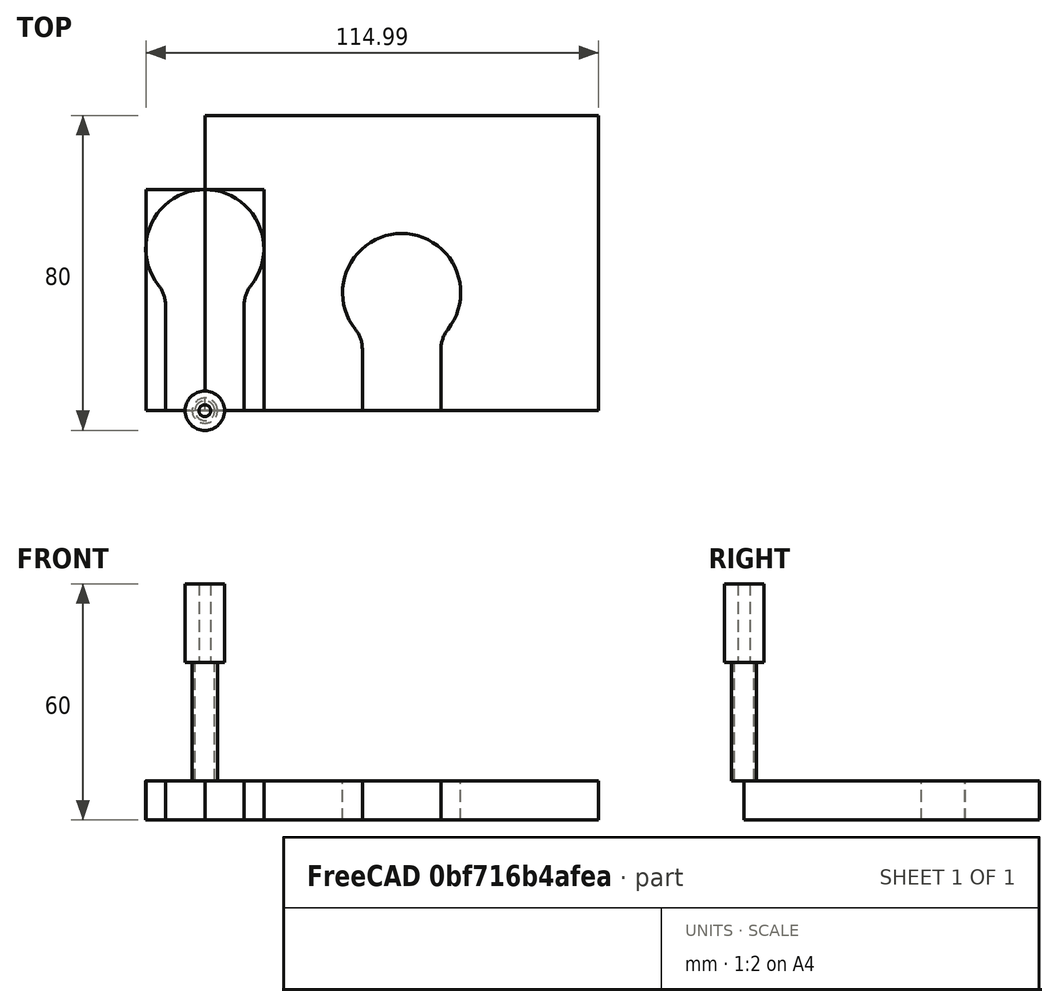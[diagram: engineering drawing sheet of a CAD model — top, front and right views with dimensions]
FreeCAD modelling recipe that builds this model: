
FCSTD DOCUMENT  (FreeCAD 0.19R14555 (Git shallow))
Label: Keyhole
License: All rights reserved
LicenseURL: http://en.wikipedia.org/wiki/All_rights_reserved
objects: Part::FeaturePython×8, Path::FeaturePython×8, App::DocumentObjectGroup×4, Sketcher::SketchObject×2, PartDesign::Pad×2, App::FeaturePython×2, PartDesign::Fillet×2, PartDesign::Body×2, App::Part×2, Path::FeatureCompoundPython×2, Mesh::FeaturePython×1
note: 23 computed .brp shape members not serialized (recipe doc carries the construction recipe); baked Part::Feature solids carry a one-line shape summary decoded from their .brp

FEATURE [Sketcher::SketchObject] Sketch
  FullyConstrained = true
  MapMode = 5
  Support = -> [XY_Plane001]
  sketch-geometry (8):
    g0: LineSegment StartX=0 StartY=75 StartZ=0 EndX=100 EndY=75 EndZ=0
    g1: LineSegment StartX=100 StartY=75 StartZ=0 EndX=100 EndY=0 EndZ=0
    g2: LineSegment StartX=100 StartY=0 StartZ=0 EndX=60 EndY=0 EndZ=0
    g3: LineSegment StartX=0 StartY=0 StartZ=0 EndX=0 EndY=75 EndZ=0
    g4: ArcOfCircle CenterX=50 CenterY=30 CenterZ=0 NormalX=0 NormalY=0 NormalZ=1 AngleXU=0 Radius=15 StartAngle=5.44212 EndAngle=10.2658
    g5: LineSegment StartX=40 StartY=0 StartZ=0 EndX=40 EndY=18.8197 EndZ=0
    g6: LineSegment StartX=60 StartY=0 StartZ=0 EndX=60 EndY=18.8197 EndZ=0
    g7: LineSegment StartX=40 StartY=0 StartZ=0 EndX=0 EndY=0 EndZ=0
  constraints (23):
    c: Coincident(g0,g1)
    c: Coincident(g1,g2)
    c: Coincident(g7,g3)
    c: Coincident(g3,g0)
    c: Horizontal(g0)
    c: Horizontal(g2)
    c: Vertical(g1)
    c: Vertical(g3)
    c: Coincident(g7,g-1)
    c: DistanceX(g7,g2) = 100
    c: DistanceY(g3,g3) = 75
    c: Diameter(g4) = 30
    c: DistanceX(g7,g4) = 50
    c: DistanceY(g7,g4) = 30
    c: Perpendicular(g2,g5)
    c: Perpendicular(g2,g6)
    c: DistanceX(g7,g5) = 40
    c: DistanceX(g7,g6) = 60
    c: Coincident(g4,g6)
    c: Coincident(g4,g5)
    c: Coincident(g2,g6)
    c: Coincident(g7,g5)
    c: Tangent(g2,g7)
FEATURE [PartDesign::Pad] Pad
  Direction = (1,1,1)
  Length = 10
  Length2 = 100
  Profile = -> Sketch
  Refine = true
  Reversed = true
  Type = 0
FEATURE [App::FeaturePython] SetupSheet  # Path/CAM operation (typed FeaturePython)
  ClearanceHeightExpression = OpStockZMax+SetupSheet.ClearanceHeightOffset
  ClearanceHeightOffset = 5
  CoolantMode = 0
  CoolantModes = None | Flood | Mist
  FinalDepthExpression = OpFinalDepth
  HorizRapid = 0
  SafeHeightExpression = OpStockZMax+SetupSheet.SafeHeightOffset
  SafeHeightOffset = 3
  StartDepthExpression = OpStartDepth
  StepDownExpression = OpToolDiameter
  VertRapid = 0
FEATURE [Part::FeaturePython] ToolBit001  label="5mm Endmill"  # Path/CAM toolbit (typed FeaturePython)
  BitPropertyNames = Chipload | CuttingEdgeHeight | Diameter | Flutes | Length | Material | ShankDiameter
  BitShape = /app/freecad/Mod/Path/Tools/Shape/endmill.fcstd
  Chipload = 0
  CuttingEdgeHeight = 30
  Diameter = 5
  File = <userpath>/Documents/CNCRouter/FreeCAD/Bit/5mm_Endmill.fctb
  Flutes = 0
  Length = 50
  Material = 0
  ShankDiameter = 3
  ShapeName = endmill
FEATURE [Path::FeaturePython] _mm_Endmill  label="5mm Endmill001"  # Path/CAM operation (typed FeaturePython)
  HorizFeed = 10
  HorizRapid = 0
  SpindleDir = 0
  SpindleSpeed = 5000
  Tool = -> ToolBit001
  ToolNumber = 1
  VertFeed = 10
  VertRapid = 0
  expr: VertRapid = SetupSheet.VertRapid
  expr: HorizRapid = SetupSheet.HorizRapid
FEATURE [Part::FeaturePython] Stock001  # WARN: FeaturePython — macro-defined, semantics opaque (R4)
  Height = 10
  Length = 100
  Placement = pos=(0,0,-10) rot=(0,0,1;0rad)
  StockType = CreateBox
  Width = 75
FEATURE [Mesh::FeaturePython] CutMaterial  # WARN: FeaturePython — macro-defined, semantics opaque (R4)
FEATURE [PartDesign::Fillet] Fillet
  Base = -> Pad [Edge20,Edge17]
  BaseFeature = -> Pad
  Radius = 8
  SupportTransform = false
FEATURE [PartDesign::Body] Body
  Group = -> [Sketch,Pad,Fillet]
  Origin = -> Origin001
  Tip = -> Fillet
FEATURE [App::Part] Part  label="Female"
  Group = -> [Body]
  Origin = -> Origin
FEATURE [Part::FeaturePython] Clone  label="Model-Part"  # Draft clone (typed FeaturePython)
  AttacherType = Attacher::AttachEngine3D
  Fuse = false
  Objects = -> [Part]
  PathResource = Model
  Scale = (1,1,1)
FEATURE [App::DocumentObjectGroup] Model
  Group = -> [Clone]
FEATURE [Sketcher::SketchObject] Sketch001
  FullyConstrained = false
  MapMode = 5
  Support = -> [XY_Plane003]
  sketch-geometry (4):
    g0: LineSegment StartX=9.995 StartY=30 StartZ=0 EndX=9.995 EndY=0 EndZ=0
    g1: LineSegment StartX=9.995 StartY=0 StartZ=0 EndX=-9.995 EndY=0 EndZ=0
    g2: LineSegment StartX=-9.995 StartY=0 StartZ=0 EndX=-9.995 EndY=30 EndZ=0
    g3: ArcOfCircle CenterX=0 CenterY=41.1781 CenterZ=0 NormalX=0 NormalY=0 NormalZ=1 AngleXU=0 Radius=14.995 StartAngle=5.44197 EndAngle=10.266
  constraints (9):
    c: Coincident(g0,g1)
    c: Coincident(g1,g2)
    c: Horizontal(g1)
    c: Vertical(g0)
    c: Vertical(g2)
    c: Symmetric(g1,g1,g-1)
    c: DistanceY(g0,g0) = 30
    c: DistanceX(g1,g1) = 19.99
    c: Diameter(g3) = 29.99
FEATURE [PartDesign::Pad] Pad001
  Direction = (1,1,1)
  Length = 10
  Length2 = 100
  Profile = -> Sketch001
  Reversed = true
  Type = 0
FEATURE [PartDesign::Fillet] Fillet001
  Base = -> Pad001 [Edge8,Edge1]
  BaseFeature = -> Pad001
  Radius = 8
  SupportTransform = false
FEATURE [PartDesign::Body] Body001
  Group = -> [Sketch001,Pad001,Fillet001]
  Origin = -> Origin003
  Tip = -> Fillet001
FEATURE [App::Part] Part001  label="Male"
  Group = -> [Body001]
  Origin = -> Origin002
FEATURE [App::FeaturePython] SetupSheet001  # Path/CAM operation (typed FeaturePython)
  ClearanceHeightExpression = OpStockZMax+SetupSheet001.ClearanceHeightOffset
  ClearanceHeightOffset = 5
  CoolantMode = 0
  CoolantModes = None | Flood | Mist
  FinalDepthExpression = OpFinalDepth
  HorizRapid = 0
  SafeHeightExpression = OpStockZMax+SetupSheet001.SafeHeightOffset
  SafeHeightOffset = 3
  StartDepthExpression = OpStartDepth
  StepDownExpression = OpToolDiameter
  VertRapid = 0
FEATURE [Part::FeaturePython] Clone001  label="Model-Male"  # Draft clone (typed FeaturePython)
  AttacherType = Attacher::AttachEngine3D
  Fuse = false
  Objects = -> [Part001]
  PathResource = Model
  Scale = (1,1,1)
FEATURE [App::DocumentObjectGroup] Model001
  Group = -> [Clone001]
FEATURE [Part::FeaturePython] Stock002  # WARN: FeaturePython — macro-defined, semantics opaque (R4)
  Height = 10
  Length = 29.98
  Placement = pos=(-14.9877,0,-10) rot=(0,0,1;0rad)
  StockType = CreateBox
  Width = 56.1423
FEATURE [Part::FeaturePython] ToolBit002  label="6.4mm Endmill"  # Path/CAM toolbit (typed FeaturePython)
  BitPropertyNames = Chipload | CuttingEdgeHeight | Diameter | Flutes | Length | Material | ShankDiameter
  BitShape = /app/freecad/Mod/Path/Tools/Shape/endmill.fcstd
  Chipload = 0
  CuttingEdgeHeight = 30
  Diameter = 6.4
  File = <userpath>/Documents/MensShed/FreeCAD/Bit/6.4mm_Endmill.fctb
  Flutes = 0
  Length = 50
  Material = 0
  ShankDiameter = 10
  ShapeName = endmill
FEATURE [Part::FeaturePython] ToolBit  label="6.4mm Endmill002"  # Path/CAM toolbit (typed FeaturePython)
  BitPropertyNames = Chipload | CuttingEdgeHeight | Diameter | Flutes | Length | Material | ShankDiameter
  BitShape = /app/freecad/Mod/Path/Tools/Shape/endmill.fcstd
  Chipload = 0
  CuttingEdgeHeight = 30
  Diameter = 6.4
  Flutes = 0
  Length = 50
  Material = 0
  ShankDiameter = 10
  ShapeName = endmill
FEATURE [Path::FeaturePython] __4mm_Endmill  label="6.4mm Endmill001"  # Path/CAM operation (typed FeaturePython)
  HorizFeed = 10
  HorizRapid = 0
  SpindleDir = 0
  SpindleSpeed = 5000
  Tool = -> ToolBit
  ToolNumber = 1
  VertFeed = 10
  VertRapid = 0
  expr: HorizRapid = SetupSheet001.HorizRapid
  expr: VertRapid = SetupSheet001.VertRapid
FEATURE [App::DocumentObjectGroup] Tools001
  Group = -> [__4mm_Endmill]
FEATURE [Path::FeaturePython] Profile001  # Path/CAM operation (typed FeaturePython)
  Active = true
  AttemptInverseAngle = false
  ClearanceHeight = 0
  Direction = 0
  EnableRotation = 0
  FinalDepth = 0
  HandleMultipleFeatures = 0
  InverseAngle = false
  JoinType = 0
  LimitDepthToFace = false
  MiterLimit = 0
  OffsetExtra = 0
  OpFinalDepth = 0
  OpStartDepth = 0
  OpStockZMax = 0
  OpStockZMin = 0
  OpToolDiameter = 0
  ReverseDirection = false
  SafeHeight = 0
  Side = 0
  StartDepth = 0
  StartPoint = (0,0,0)
  StepDown = 0
  UseComp = false
  UseStartPoint = false
  processCircles = false
  processHoles = false
  processPerimeter = false
FEATURE [Path::FeaturePython] Profile002  # Path/CAM operation (typed FeaturePython)
  Active = true
  AreaParams:
    Tolerance = 1e-07
    FitArcs = True
    Simplify = False
    CleanDistance = 0.0
    Accuracy = 0.01
    Unit = 1.0
    MinArcPoints = 4
    MaxArcPoints = 100
    ClipperScale = 10000000.0
    Fill = 0
    Coplanar = 0
    Reorient = True
    Outline = False
    Explode = False
    OpenMode = 0
    Deflection = 0.01
    SubjectFill = 0
    ClipFill = 0
    Offset = 3.2
    ExtraPass = 0
    Stepover = 0.0
    LastStepover = 0.0
    JoinType = 0
    EndType = 0
    MiterLimit = 2.0
    RoundPrecision = 0.0
    PocketMode = 0
    ToolRadius = 1.0
    PocketExtraOffset = 0.0
    PocketStepover = 0.0
    PocketLastStepover = 0.0
    FromCenter = False
    Angle = 45.0
    AngleShift = 0.0
    Shift = 0.0
    Thicken = False
    SectionCount = -1
    Stepdown = 1.0
    SectionOffset = 0.0
    SectionTolerance = 1e-06
    SectionMode = 2
    Project = False
  AttemptInverseAngle = true
  Base = -> [Clone001]
  ClearanceHeight = 5
  CoolantMode = None
  CycleTime = 00:01:04
  Direction = 0
  EnableRotation = 0
  FinalDepth = -10
  HandleMultipleFeatures = 0
  InverseAngle = false
  JoinType = 0
  LimitDepthToFace = true
  MiterLimit = 0.1
  OffsetExtra = 0
  OpFinalDepth = 0
  OpStartDepth = 3
  OpStockZMax = 0
  OpStockZMin = -10
  OpToolDiameter = 6.4
  PathParams = {'orientation': 1, 'feedrate': 10.0, 'feedrate_v': 10.0, 'verbose': True, 'resume_height': 3.0, 'retraction': 5.0, 'return_end': True, 'preamble': False}
  ReverseDirection = false
  SafeHeight = 3
  Side = 0
  StartDepth = 0
  StartPoint = (0,0,0)
  StepDown = 3
  ToolController = -> __4mm_Endmill
  UseComp = true
  UseStartPoint = false
  processCircles = false
  processHoles = false
  processPerimeter = true
  expr: ClearanceHeight = OpStockZMax + SetupSheet001.ClearanceHeightOffset
  expr: SafeHeight = OpStockZMax + SetupSheet001.SafeHeightOffset
  expr: StepDown = 3
  expr: FinalDepth = -10
  expr: StartDepth = 0
FEATURE [Path::FeatureCompoundPython] Operations001  # Path/CAM operation (typed FeaturePython)
  Group = -> [Profile002]
  UsePlacements = false
FEATURE [Path::FeaturePython] Job001  # Path/CAM operation (typed FeaturePython)
  CycleTime = 00:01:04
  Fixtures = G54
  GeometryTolerance = 0.01
  LastPostProcessDate = 2021-12-07 20:45:51.677098
  LastPostProcessOutput = <userpath>/Documents/MensShed/KeyholeMale.ngc
  Model = -> Model001
  Operations = -> Operations001
  OrderOutputBy = 0
  PostProcessor = 7
  PostProcessorOutputFile = <userpath>/Documents/MensShed/KeyholeMale.ngc
  SetupSheet = -> SetupSheet001
  SplitOutput = false
  Stock = -> Stock002
  Tools = -> Tools001
FEATURE [Part::FeaturePython] ToolBit003  label="6.4mm Endmill003"  # Path/CAM toolbit (typed FeaturePython)
  BitPropertyNames = Chipload | CuttingEdgeHeight | Diameter | Flutes | Length | Material | ShankDiameter
  BitShape = /app/freecad/Mod/Path/Tools/Shape/endmill.fcstd
  Chipload = 0
  CuttingEdgeHeight = 30
  Diameter = 6.4
  File = <userpath>/Documents/MensShed/FreeCAD/Bit/6.4mm_Endmill.fctb
  Flutes = 0
  Length = 50
  Material = 0
  ShankDiameter = 10
  ShapeName = endmill
FEATURE [Path::FeaturePython] __4mm_Endmill003  label="6.4mm Endmill004"  # Path/CAM operation (typed FeaturePython)
  HorizFeed = 10
  HorizRapid = 0
  SpindleDir = 0
  SpindleSpeed = 5000
  Tool = -> ToolBit003
  ToolNumber = 1
  VertFeed = 10
  VertRapid = 0
  expr: HorizRapid = SetupSheet.HorizRapid
  expr: VertRapid = SetupSheet.VertRapid
FEATURE [App::DocumentObjectGroup] Tools
  Group = -> [_mm_Endmill,__4mm_Endmill003]
FEATURE [Path::FeaturePython] Profile  # Path/CAM operation (typed FeaturePython)
  Active = true
  AreaParams:
    Tolerance = 1e-07
    FitArcs = True
    Simplify = False
    CleanDistance = 0.0
    Accuracy = 0.01
    Unit = 1.0
    MinArcPoints = 4
    MaxArcPoints = 100
    ClipperScale = 10000000.0
    Fill = 0
    Coplanar = 0
    Reorient = True
    Outline = False
    Explode = False
    OpenMode = 0
    Deflection = 0.01
    SubjectFill = 0
    ClipFill = 0
    Offset = 2.5
    ExtraPass = 0
    Stepover = 0.0
    LastStepover = 0.0
    JoinType = 0
    EndType = 0
    MiterLimit = 2.0
    RoundPrecision = 0.0
    PocketMode = 0
    ToolRadius = 1.0
    PocketExtraOffset = 0.0
    PocketStepover = 0.0
    PocketLastStepover = 0.0
    FromCenter = False
    Angle = 45.0
    AngleShift = 0.0
    Shift = 0.0
    Thicken = False
    SectionCount = -1
    Stepdown = 1.0
    SectionOffset = 0.0
    SectionTolerance = 1e-06
    SectionMode = 2
    Project = False
  AttemptInverseAngle = true
  Base = -> [Clone]
  ClearanceHeight = 5
  CoolantMode = None
  CycleTime = 00:00:00
  Direction = 0
  EnableRotation = 0
  FinalDepth = -10
  HandleMultipleFeatures = 0
  InverseAngle = false
  JoinType = 0
  LimitDepthToFace = true
  MiterLimit = 0.1
  OffsetExtra = 0
  OpFinalDepth = -10
  OpStartDepth = 0
  OpStockZMax = 0
  OpStockZMin = -10
  OpToolDiameter = 6.4
  PathParams = {'orientation': 1, 'feedrate': 10.0, 'feedrate_v': 10.0, 'verbose': True, 'resume_height': 3.0, 'retraction': 5.0, 'return_end': True, 'preamble': False}
  ReverseDirection = false
  SafeHeight = 3
  Side = 0
  StartDepth = 0
  StartPoint = (0,0,0)
  StepDown = 3
  ToolController = -> __4mm_Endmill003
  UseComp = true
  UseStartPoint = false
  processCircles = false
  processHoles = false
  processPerimeter = true
  expr: StartDepth = 0
  expr: FinalDepth = -10
  expr: StepDown = 3
  expr: SafeHeight = OpStockZMax + SetupSheet.SafeHeightOffset
  expr: ClearanceHeight = OpStockZMax + SetupSheet.ClearanceHeightOffset
FEATURE [Path::FeatureCompoundPython] Operations  # Path/CAM operation (typed FeaturePython)
  Group = -> [Profile]
  UsePlacements = false
FEATURE [Path::FeaturePython] Job  # Path/CAM operation (typed FeaturePython)
  CycleTime = 00:00:00
  Fixtures = G54
  GeometryTolerance = 0.01
  LastPostProcessDate = 2021-12-07 20:45:37.349971
  LastPostProcessOutput = <userpath>/Documents/MensShed/Keyhole.ngc
  Model = -> Model
  Operations = -> Operations
  OrderOutputBy = 0
  PostProcessor = 7
  PostProcessorOutputFile = <userpath>/Documents/MensShed/Keyhole.ngc
  SetupSheet = -> SetupSheet
  SplitOutput = false
  Stock = -> Stock001
  Tools = -> Tools
